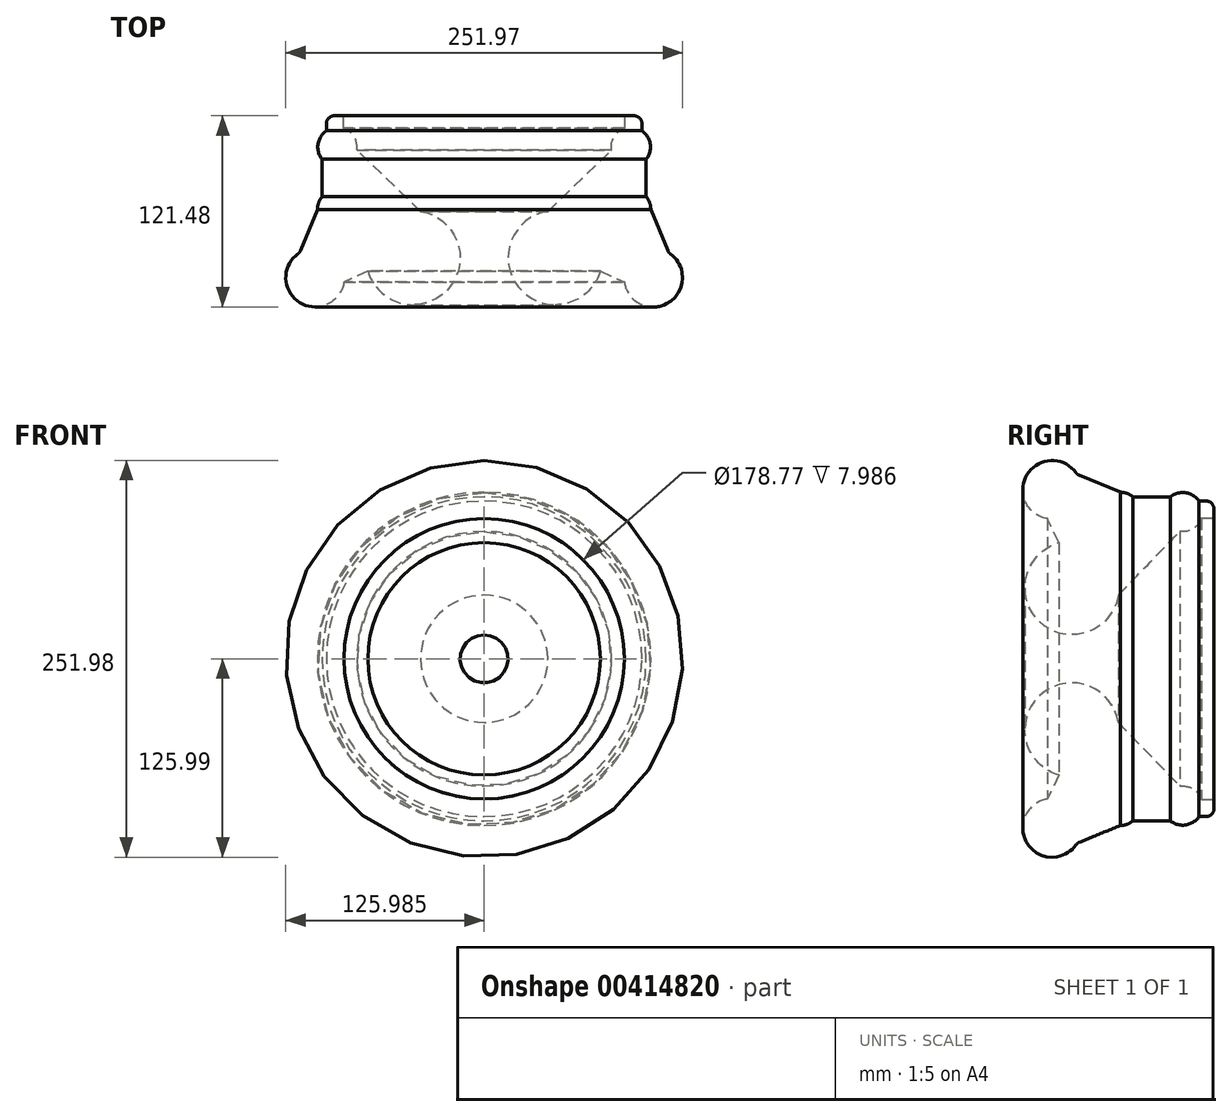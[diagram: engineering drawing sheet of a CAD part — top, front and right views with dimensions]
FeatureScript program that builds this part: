
annotation { "Feature Type Name" : "Feature", "Feature Type Description" : "" }
export const myFeature = defineFeature(function(context is Context, id is Id, definition is map)
    precondition{}
    {
        {
            var Q0;
            Q0=qCreatedBy(makeId("Top.planeOp"),FACE);
            var sketch = newSketch(context, id + "F0", { "sketchPlane" : qUnion([Q0])});
            skCircle(sketch, "E0", {"center": v(0, 48.73) * mm, "radius": 12.46 * mm});
            skCircle(sketch, "E1", {"center": v(-48.08, -21.66) * mm, "radius": 29.87 * mm});
            skCircle(sketch, "E2", {"center": v(0, 9.02) * mm, "radius": 12.67 * mm});
            skCircle(sketch, "E3", {"center": v(14.19, -34.29) * mm, "radius": 18.6 * mm});
            skLineSegment(sketch, "E4", {"start": v(-12.32, 46.84) * mm, "end": v(-52.78, 7.84) * mm});
            skLineSegment(sketch, "E5", {"start": v(-9.37, 40.52) * mm, "end": v(-42.56, 7.7) * mm});
            skLineSegment(sketch, "E6", {"start": v(-27.5, 0) * mm, "end": v(-12.03, 5.07) * mm});
            skLineSegment(sketch, "E7", {"start": v(-23.32, -4.94) * mm, "end": v(-8.89, 0) * mm});
            skLineSegment(sketch, "E8", {"start": v(-18.6, -16.77) * mm, "end": v(-2.92, -26.96) * mm});
            skLineSegment(sketch, "E9", {"start": v(-19.4, -30.02) * mm, "end": v(-4.2, -37.17) * mm});
            skLineSegment(sketch, "E10", {"start": v(18.64, -16.22) * mm, "end": v(10.5, 0) * mm});
            skLineSegment(sketch, "E11", {"start": v(24.02, -18.5) * mm, "end": v(12.67, 9) * mm});
            skLineSegment(sketch, "E12", {"start": v(9.7, 17.17) * mm, "end": v(9.7, 40.9) * mm});
            skLineSegment(sketch, "E13", {"start": v(6.3, 37.97) * mm, "end": v(6.3, 20.02) * mm});
            skLineSegment(sketch, "E14", {"start": v(-93.2, 71.29) * mm, "end": v(-93.2, -53.24) * mm});
            skLineSegment(sketch, "E15.bottom", {"start": v(-3.8, 68.58) * mm, "end": v(7.01, 68.58) * mm});
            skLineSegment(sketch, "E15.left", {"start": v(-3.8, 68.58) * mm, "end": v(-3.8, 60.6) * mm});
            skLineSegment(sketch, "E15.right", {"start": v(7.01, 68.58) * mm, "end": v(7.01, 59.03) * mm});
            skSolve(sketch);
        }
        {
            var Q0;
            Q0=makeQuery(id+"F0.imprint","IMPRINT",FACE,{"disambiguationData":[TD([[makeQuery(id+"F0.imprint","IMPRINT",EDGE,{"derivedFrom":sQuery(id+"F0.wireOp",EDGE,"E15.bottom")}),-1.0]])]});
            var Q1;
            {var subQ0=sQuery(id+"F0.wireOp",EDGE,"E3");var subQ1=makeQuery(id+"F0.imprint","IMPRINT",VERTEX,{"derivedFrom":subQ0});Q1=makeQuery(id+"F0.imprint","IMPRINT",FACE,{"disambiguationData":[TD([[makeQuery(id+"F0.imprint","IMPRINT",EDGE,{"disambiguationData":[TD([[subQ1,1.0]])],"derivedFrom":subQ0}),1.0]])]});}
            var Q2;
            {var subQ0=sQuery(id+"F0.wireOp",EDGE,"E4");Q2=makeQuery(id+"F0.imprint","IMPRINT",FACE,{"disambiguationData":[TD([[makeQuery(id+"F0.imprint","IMPRINT",EDGE,{"derivedFrom":subQ0}),1.0]])]});}
            var Q3;
            {var subQ0=sQuery(id+"F0.wireOp",EDGE,"E12");Q3=makeQuery(id+"F0.imprint","IMPRINT",FACE,{"disambiguationData":[TD([[makeQuery(id+"F0.imprint","IMPRINT",EDGE,{"derivedFrom":subQ0}),1.0]])]});}
            var Q4;
            {var subQ0=sQuery(id+"F0.wireOp",EDGE,"E8");Q4=makeQuery(id+"F0.imprint","IMPRINT",FACE,{"disambiguationData":[TD([[makeQuery(id+"F0.imprint","IMPRINT",EDGE,{"derivedFrom":subQ0}),-1.0]])]});}
            var Q5;
            {var subQ0=sQuery(id+"F0.wireOp",EDGE,"E0");var subQ4=makeQuery(id+"F0.imprint","INTERSECT",VERTEX,{"derivedFrom":[subQ0,sQuery(id+"F0.wireOp",EDGE,"E15.left")]});Q5=makeQuery(id+"F0.imprint","IMPRINT",FACE,{"disambiguationData":[TD([[makeQuery(id+"F0.imprint","IMPRINT",EDGE,{"disambiguationData":[TD([[subQ4,1.0]])],"derivedFrom":subQ0}),1.0]])]});}
            var Q6;
            {var subQ0=sQuery(id+"F0.wireOp",EDGE,"E6");Q6=makeQuery(id+"F0.imprint","IMPRINT",FACE,{"disambiguationData":[TD([[makeQuery(id+"F0.imprint","IMPRINT",EDGE,{"derivedFrom":subQ0}),-1.0]])]});}
            var Q7;
            {var subQ0=sQuery(id+"F0.wireOp",EDGE,"E2");var subQ5=makeQuery(id+"F0.imprint","INTERSECT",VERTEX,{"derivedFrom":[subQ0,sQuery(id+"F0.wireOp",EDGE,"E12")]});Q7=makeQuery(id+"F0.imprint","IMPRINT",FACE,{"disambiguationData":[TD([[makeQuery(id+"F0.imprint","IMPRINT",EDGE,{"disambiguationData":[TD([[subQ5,-1.0]])],"derivedFrom":subQ0}),1.0]])]});}
            var Q8;
            {var subQ0=sQuery(id+"F0.wireOp",EDGE,"E1");var subQ4=makeQuery(id+"F0.imprint","INTERSECT",VERTEX,{"derivedFrom":[subQ0,sQuery(id+"F0.wireOp",EDGE,"E7")]});Q8=makeQuery(id+"F0.imprint","IMPRINT",FACE,{"disambiguationData":[TD([[makeQuery(id+"F0.imprint","IMPRINT",EDGE,{"disambiguationData":[TD([[subQ4,1.0]])],"derivedFrom":subQ0}),1.0]])]});}
            var Q9;
            {var subQ4=sQuery(id+"F0.wireOp",EDGE,"E7");Q9=makeQuery(id+"F0.imprint","IMPRINT",FACE,{"disambiguationData":[TD([[makeQuery(id+"F0.imprint","IMPRINT",EDGE,{"derivedFrom":subQ4}),-1.0]])]});}
            var Q10;
            {var subQ0=sQuery(id+"F0.wireOp",EDGE,"E5");Q10=makeQuery(id+"F0.imprint","IMPRINT",FACE,{"disambiguationData":[TD([[makeQuery(id+"F0.imprint","IMPRINT",EDGE,{"derivedFrom":subQ0}),1.0]])]});}
            var Q11;
            Q11=sQuery(id+"F0.wireOp",EDGE,"E14");
            revolve(context, id + "F1", {"entities" : qUnion([Q0, Q1, Q2, Q3, Q4, Q5, Q6, Q7, Q8, Q9, Q10]), "axis" : qUnion([Q11]), "revolveType" : RevolveType.FULL});
        }
        {
            var Q0;
            Q0=makeQuery(id+"F1.opRevolve","SWEPT_EDGE",EDGE,{"disambiguationData":[OSD([sQuery(id+"F0.wireOp",EDGE,"E15.bottom"),sQuery(id+"F0.wireOp",EDGE,"E15.right")])]});
            fillet(context, id + "F2", {"entities" : qUnion([Q0]), "radius" : 5.08 * mm, "tangentPropagation" : true, "allowEdgeOverflow" : false});
        }
        {
            var Q0;
            Q0=makeQuery(id+"F1.opRevolve","SWEPT_EDGE",EDGE,{"disambiguationData":[OSD([sQuery(id+"F0.wireOp",EDGE,"E3"),sQuery(id+"F0.wireOp",EDGE,"E11")])]});
            fillet(context, id + "F3", {"entities" : qUnion([Q0]), "radius" : 5.08 * mm, "tangentPropagation" : true, "allowEdgeOverflow" : false});
        }
    });
